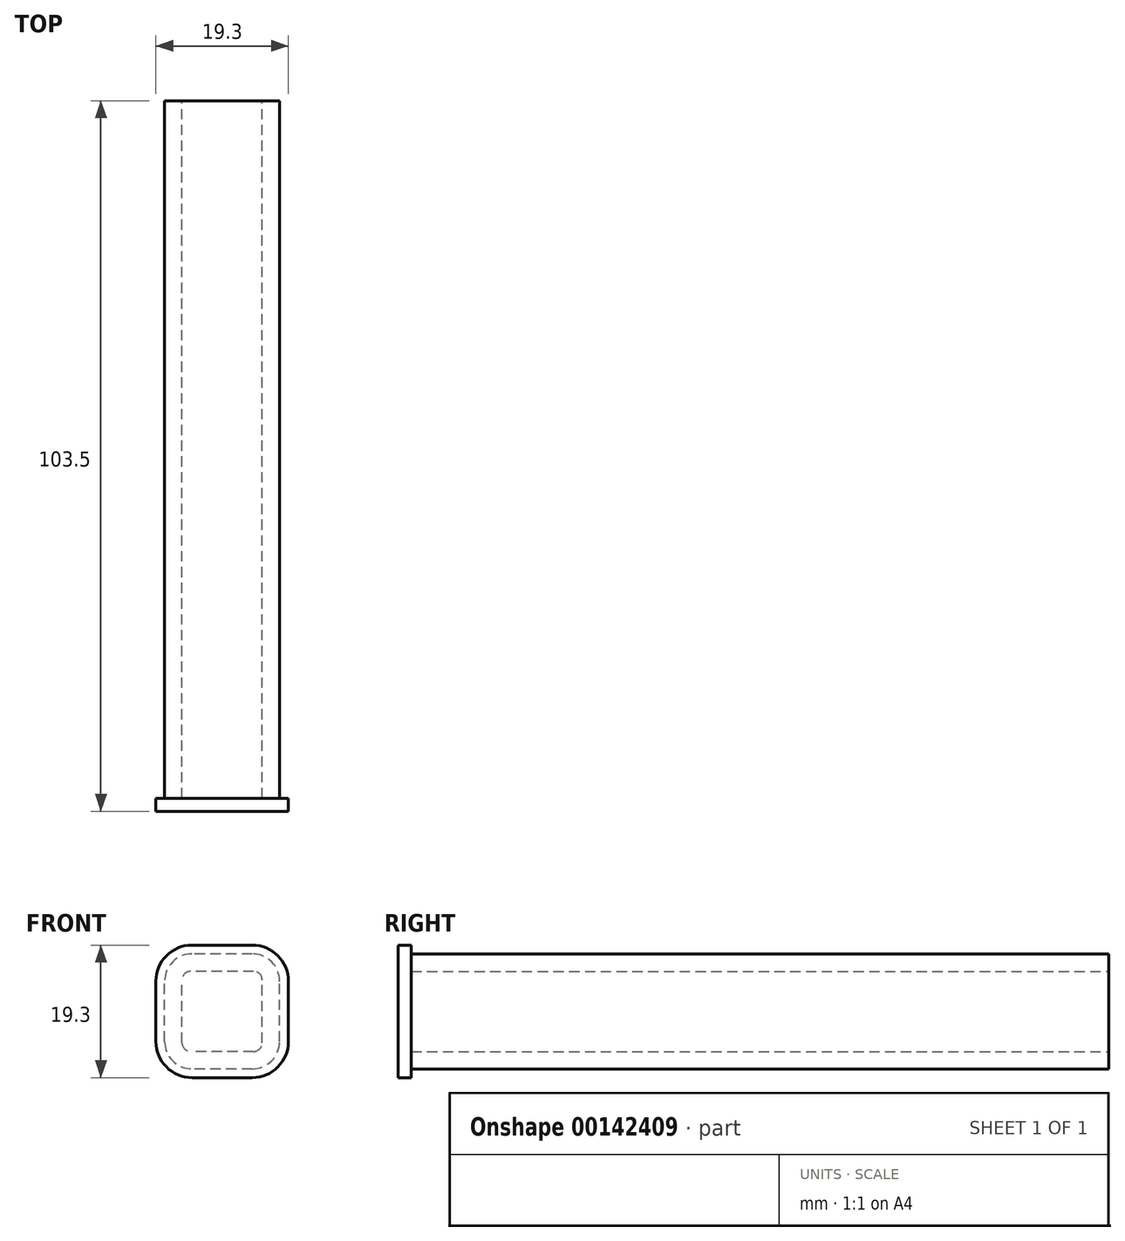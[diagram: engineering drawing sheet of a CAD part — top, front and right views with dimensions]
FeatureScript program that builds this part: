
annotation { "Feature Type Name" : "Feature", "Feature Type Description" : "" }
export const myFeature = defineFeature(function(context is Context, id is Id, definition is map)
    precondition{}
    {
        {
            var Q0;
            Q0=qCreatedBy(makeId("Front.planeOp"),FACE);
            var sketch = newSketch(context, id + "F0", { "sketchPlane" : qUnion([Q0])});
            skLineSegment(sketch, "E0.bottom", {"start": v(4.38, -8.38) * mm, "end": v(-4.38, -8.38) * mm});
            skLineSegment(sketch, "E0.top", {"start": v(4.38, 8.38) * mm, "end": v(-4.38, 8.38) * mm});
            skLineSegment(sketch, "E0.left", {"start": v(8.38, -4.38) * mm, "end": v(8.38, 4.38) * mm});
            skLineSegment(sketch, "E0.right", {"start": v(-8.38, -4.38) * mm, "end": v(-8.38, 4.38) * mm});
            skPoint(sketch, "E0.middle", {"position": v(0, 0) * mm});
            skLineSegment(sketch, "E1.0", {"start": v(4.57, 5.84) * mm, "end": v(-4.57, 5.84) * mm});
            skLineSegment(sketch, "E1.1", {"start": v(5.84, -4.57) * mm, "end": v(5.84, 4.57) * mm});
            skLineSegment(sketch, "E1.2", {"start": v(4.57, -5.84) * mm, "end": v(-4.57, -5.84) * mm});
            skLineSegment(sketch, "E1.3", {"start": v(-5.84, -4.57) * mm, "end": v(-5.84, 4.57) * mm});
            skPoint(sketch, "E2.visualSharp", {"position": v(-8.38, 8.38) * mm});
            skArc(sketch, "E2.filletArc", {"start": v(-4.38, 8.38) * mm, "mid": v(-7.21, 7.21) * mm, "end": v(-8.38, 4.38) * mm});
            skPoint(sketch, "E3.visualSharp", {"position": v(8.38, 8.38) * mm});
            skArc(sketch, "E3.filletArc", {"start": v(8.38, 4.38) * mm, "mid": v(7.21, 7.21) * mm, "end": v(4.38, 8.38) * mm});
            skPoint(sketch, "E4.visualSharp", {"position": v(8.38, -8.38) * mm});
            skArc(sketch, "E4.filletArc", {"start": v(4.38, -8.38) * mm, "mid": v(7.21, -7.21) * mm, "end": v(8.38, -4.38) * mm});
            skPoint(sketch, "E5.visualSharp", {"position": v(-8.38, -8.38) * mm});
            skArc(sketch, "E5.filletArc", {"start": v(-8.38, -4.38) * mm, "mid": v(-7.21, -7.21) * mm, "end": v(-4.38, -8.38) * mm});
            skPoint(sketch, "E6.visualSharp", {"position": v(-5.84, 5.84) * mm});
            skArc(sketch, "E6.filletArc", {"start": v(-4.57, 5.84) * mm, "mid": v(-5.47, 5.47) * mm, "end": v(-5.84, 4.57) * mm});
            skPoint(sketch, "E7.visualSharp", {"position": v(5.84, 5.84) * mm});
            skArc(sketch, "E7.filletArc", {"start": v(5.84, 4.57) * mm, "mid": v(5.47, 5.47) * mm, "end": v(4.57, 5.84) * mm});
            skPoint(sketch, "E8.visualSharp", {"position": v(5.84, -5.84) * mm});
            skArc(sketch, "E8.filletArc", {"start": v(4.57, -5.84) * mm, "mid": v(5.47, -5.47) * mm, "end": v(5.84, -4.57) * mm});
            skPoint(sketch, "E9.visualSharp", {"position": v(-5.84, -5.84) * mm});
            skArc(sketch, "E9.filletArc", {"start": v(-5.84, -4.57) * mm, "mid": v(-5.47, -5.47) * mm, "end": v(-4.57, -5.84) * mm});
            skSolve(sketch);
        }
        {
            var Q0;
            Q0=makeQuery(id+"F0.imprint","IMPRINT",FACE,{"disambiguationData":[TD([[makeQuery(id+"F0.imprint","IMPRINT",EDGE,{"derivedFrom":sQuery(id+"F0.wireOp",EDGE,"E0.bottom")}),-1.0]])]});
            extrude(context, id + "F1", {"entities" : qUnion([Q0]), "depth" : 101.6 * mm, "offsetDistance" : 25.4 * mm});
        }
        {
            var Q0;
            Q0=makeQuery(id+"F1.opExtrude","CAP_FACE",FACE,{"disambiguationData":[OSD([sQuery(id+"F0.wireOp",EDGE,"E0.bottom"),sQuery(id+"F0.wireOp",EDGE,"E0.top"),sQuery(id+"F0.wireOp",EDGE,"E0.left"),sQuery(id+"F0.wireOp",EDGE,"E0.right"),sQuery(id+"F0.wireOp",EDGE,"E1.0"),sQuery(id+"F0.wireOp",EDGE,"E1.1"),sQuery(id+"F0.wireOp",EDGE,"E1.2"),sQuery(id+"F0.wireOp",EDGE,"E1.3"),sQuery(id+"F0.wireOp",EDGE,"E2.filletArc"),sQuery(id+"F0.wireOp",EDGE,"E3.filletArc"),sQuery(id+"F0.wireOp",EDGE,"E4.filletArc"),sQuery(id+"F0.wireOp",EDGE,"E5.filletArc"),sQuery(id+"F0.wireOp",EDGE,"E6.filletArc"),sQuery(id+"F0.wireOp",EDGE,"E7.filletArc"),sQuery(id+"F0.wireOp",EDGE,"E8.filletArc"),sQuery(id+"F0.wireOp",EDGE,"E9.filletArc")])],"isStart":false});
            var sketch = newSketch(context, id + "F2", { "sketchPlane" : qUnion([Q0])});
            skLineSegment(sketch, "E10.bottom", {"start": v(4.4, -9.65) * mm, "end": v(-4.4, -9.65) * mm});
            skLineSegment(sketch, "E10.top", {"start": v(4.4, 9.65) * mm, "end": v(-4.4, 9.65) * mm});
            skLineSegment(sketch, "E10.left", {"start": v(9.65, -4.4) * mm, "end": v(9.65, 4.4) * mm});
            skLineSegment(sketch, "E10.right", {"start": v(-9.65, -4.4) * mm, "end": v(-9.65, 4.4) * mm});
            skPoint(sketch, "E10.middle", {"position": v(0, 0) * mm});
            skPoint(sketch, "E11.visualSharp", {"position": v(-9.65, 9.65) * mm});
            skArc(sketch, "E11.filletArc", {"start": v(-4.4, 9.65) * mm, "mid": v(-8.11, 8.11) * mm, "end": v(-9.65, 4.4) * mm});
            skPoint(sketch, "E12.visualSharp", {"position": v(9.65, 9.65) * mm});
            skArc(sketch, "E12.filletArc", {"start": v(9.65, 4.4) * mm, "mid": v(8.11, 8.11) * mm, "end": v(4.4, 9.65) * mm});
            skPoint(sketch, "E13.visualSharp", {"position": v(9.65, -9.65) * mm});
            skArc(sketch, "E13.filletArc", {"start": v(4.4, -9.65) * mm, "mid": v(8.11, -8.11) * mm, "end": v(9.65, -4.4) * mm});
            skPoint(sketch, "E14.visualSharp", {"position": v(-9.65, -9.65) * mm});
            skArc(sketch, "E14.filletArc", {"start": v(-9.65, -4.4) * mm, "mid": v(-8.11, -8.11) * mm, "end": v(-4.4, -9.65) * mm});
            skSolve(sketch);
        }
        {
            var Q0;
            Q0=makeQuery(id+"F2.imprint","IMPRINT",FACE,{"disambiguationData":[TD([[makeQuery(id+"F2.imprint","IMPRINT",EDGE,{"derivedFrom":sQuery(id+"F2.wireOp",EDGE,"E10.bottom")}),-1.0]])]});
            var Q1;
            Q1=makeQuery(id+"F2.imprint","IMPRINT",FACE,{"disambiguationData":[TD([[makeQuery(id+"F2.imprint","IMPRINT",EDGE,{"derivedFrom":makeQuery(id+"F1.opExtrude","CAP_EDGE",EDGE,{"disambiguationData":[OSD([sQuery(id+"F0.wireOp",EDGE,"E0.bottom")])],"isStart":false})}),-1.0]])]});
            var Q2;
            Q2=makeQuery(id+"F2.imprint","IMPRINT",FACE,{"disambiguationData":[TD([[makeQuery(id+"F2.imprint","IMPRINT",EDGE,{"derivedFrom":makeQuery(id+"F1.opExtrude","CAP_EDGE",EDGE,{"disambiguationData":[OSD([sQuery(id+"F0.wireOp",EDGE,"E1.0")])],"isStart":false})}),1.0]])]});
            extrude(context, id + "F3", {"entities" : qUnion([Q0, Q1, Q2]), "operationType" : NewBodyOperationType.ADD, "depth" : 1.9 * mm, "offsetDistance" : 25.4 * mm});
        }
    });
